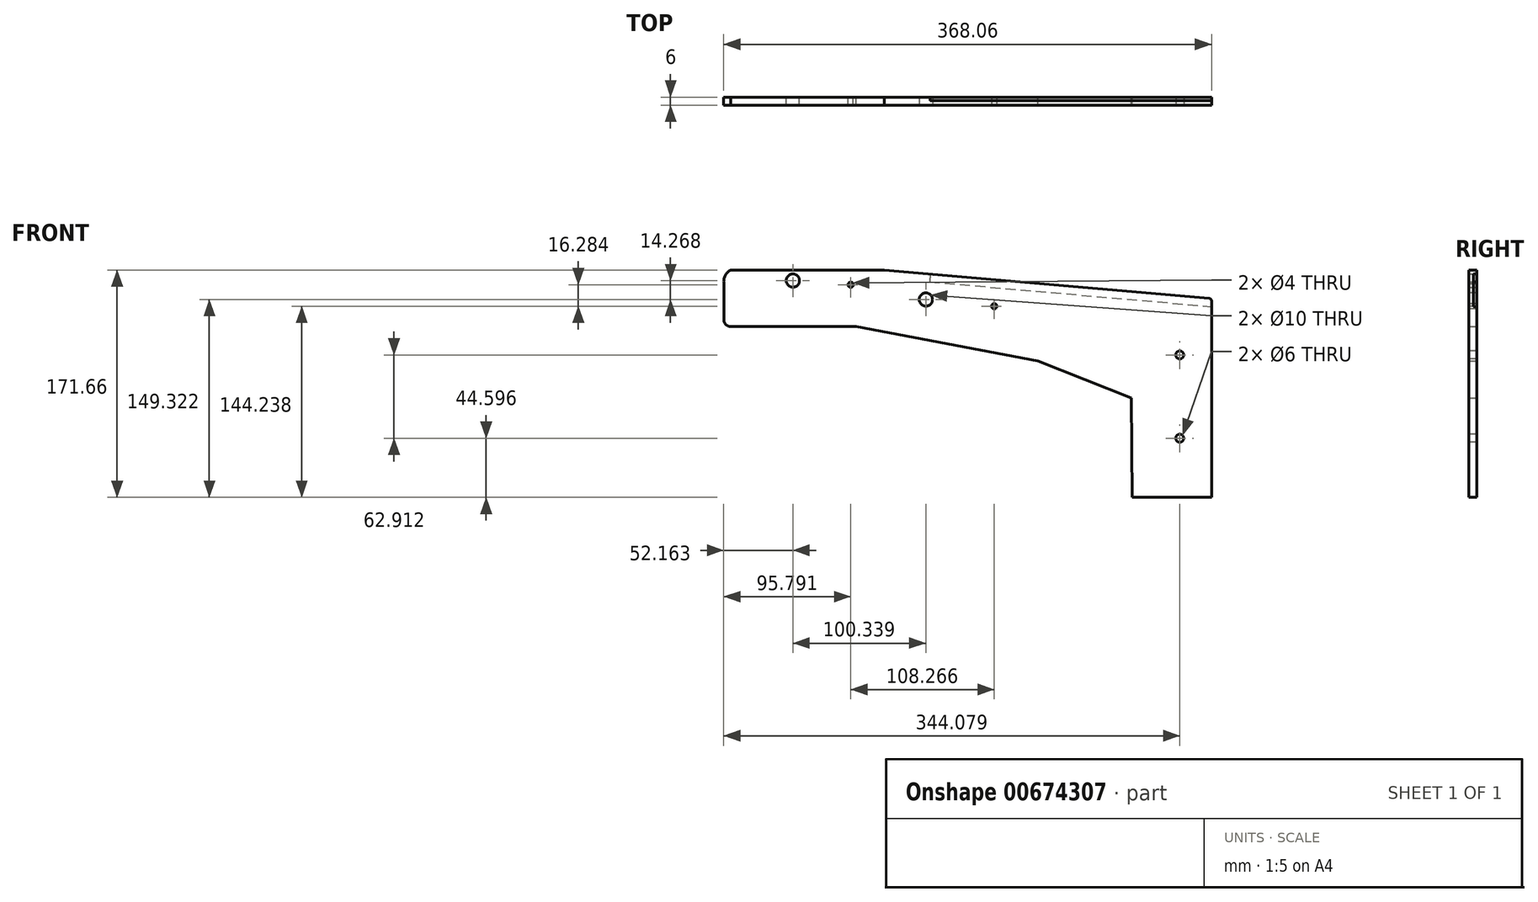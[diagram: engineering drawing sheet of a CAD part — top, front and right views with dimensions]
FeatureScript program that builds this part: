
annotation { "Feature Type Name" : "Feature", "Feature Type Description" : "" }
export const myFeature = defineFeature(function(context is Context, id is Id, definition is map)
    precondition{}
    {
        {
            var Q0;
            Q0=qCreatedBy(makeId("Front.planeOp"),FACE);
            var sketch = newSketch(context, id + "F0", { "sketchPlane" : qUnion([Q0])});
            skArc(sketch, "E0", {"start": v(-54.77, 8.07) * mm, "mid": v(-58.95, 3.73) * mm, "end": v(-59.88, -2.22) * mm});
            skLineSegment(sketch, "E1", {"start": v(-38.64, -34.67) * mm, "end": v(39.88, -34.67) * mm});
            skLineSegment(sketch, "E2", {"start": v(308.06, -13.59) * mm, "end": v(308.06, -163.59) * mm});
            skLineSegment(sketch, "E3", {"start": v(308.06, -163.59) * mm, "end": v(248.06, -163.59) * mm});
            skLineSegment(sketch, "E4", {"start": v(-59.88, -2.22) * mm, "end": v(-59.88, -29.67) * mm});
            skLineSegment(sketch, "E5", {"start": v(-54.88, -34.67) * mm, "end": v(-38.64, -34.67) * mm});
            skPoint(sketch, "E6.visualSharp", {"position": v(-59.88, -34.67) * mm});
            skArc(sketch, "E6.filletArc", {"start": v(-59.88, -29.67) * mm, "mid": v(-58.42, -33.2) * mm, "end": v(-54.88, -34.67) * mm});
            skPoint(sketch, "E7", {"position": v(35.8, -3.07) * mm});
            skCircle(sketch, "E8", {"center": v(35.8, -3.07) * mm, "radius": 2 * mm});
            skLineSegment(sketch, "E9", {"start": v(248.06, -163.59) * mm, "end": v(247.38, -88.6) * mm});
            skLineSegment(sketch, "E10", {"start": v(177.12, -60.52) * mm, "end": v(247.38, -88.6) * mm});
            skLineSegment(sketch, "E11", {"start": v(39.88, -34.67) * mm, "end": v(177.12, -60.52) * mm});
            skLineSegment(sketch, "E12", {"start": v(308.06, -13.59) * mm, "end": v(61.1, 8.07) * mm});
            skLineSegment(sketch, "E13", {"start": v(61.1, 8.07) * mm, "end": v(-54.77, 8.07) * mm});
            skSolve(sketch);
        }
        {
            var Q0;
            Q0=qSketchRegion(id+"F0",true);
            extrude(context, id + "F1", {"entities" : qUnion([Q0]), "depth" : 6 * mm, "offsetDistance" : 25 * mm});
        }
        {
            var Q0;
            Q0=makeQuery(id+"F1.opExtrude","CAP_FACE",FACE,{"disambiguationData":[OSD([sQuery(id+"F0.wireOp",EDGE,"69VMhtjD-FHem-1Nzl-ZIln-yZqZocFnkeLI"),sQuery(id+"F0.wireOp",EDGE,"E0"),sQuery(id+"F0.wireOp",EDGE,"E1"),sQuery(id+"F0.wireOp",EDGE,"E2"),sQuery(id+"F0.wireOp",EDGE,"E3"),sQuery(id+"F0.wireOp",EDGE,"zyuM4KxI-rK7D-eBj5-RQWG-Z7kNhVQKbpSr"),sQuery(id+"F0.wireOp",EDGE,"E4"),sQuery(id+"F0.wireOp",EDGE,"E5"),sQuery(id+"F0.wireOp",EDGE,"E6.filletArc"),sQuery(id+"F0.wireOp",EDGE,"Sq1smuhl-J9rg-3BfP-JIUe-rn6nJ9PzM2vD"),sQuery(id+"F0.wireOp",EDGE,"PUNmVgVp-qFH2-CwZl-KZ4H-ZFihZqVa5LSU"),sQuery(id+"F0.wireOp",EDGE,"RsVNkQyW-0Ggk-FljP-8XP7-kQ1KxApps7TM")])],"isStart":false});
            var sketch = newSketch(context, id + "F2", { "sketchPlane" : qUnion([Q0])});
            skLineSegment(sketch, "E14", {"start": v(-49.88, 0) * mm, "end": v(-59.97, 0) * mm});
            skLineSegment(sketch, "E15", {"start": v(-49.88, 0) * mm, "end": v(30.12, 0) * mm});
            skLineSegment(sketch, "E16", {"start": v(30.12, 0) * mm, "end": v(92.5, -8.77) * mm});
            skLineSegment(sketch, "E17", {"start": v(92.5, -8.77) * mm, "end": v(92.5, -14.27) * mm});
            skCircle(sketch, "E18", {"center": v(92.5, -14.27) * mm, "radius": 5 * mm});
            skSolve(sketch);
        }
        {
            var Q0;
            Q0=qSketchRegion(id+"F2",true);
            extrude(context, id + "F3", {"entities" : qUnion([Q0]), "operationType" : NewBodyOperationType.REMOVE, "endBound" : BoundingType.THROUGH_ALL, "oppositeDirection" : true, "depth" : 25 * mm, "offsetDistance" : 25 * mm});
        }
        {
            var Q0;
            Q0=makeQuery(id+"F1.opExtrude","CAP_FACE",FACE,{"disambiguationData":[OSD([sQuery(id+"F0.wireOp",EDGE,"69VMhtjD-FHem-1Nzl-ZIln-yZqZocFnkeLI"),sQuery(id+"F0.wireOp",EDGE,"E0"),sQuery(id+"F0.wireOp",EDGE,"E1"),sQuery(id+"F0.wireOp",EDGE,"E2"),sQuery(id+"F0.wireOp",EDGE,"E3"),sQuery(id+"F0.wireOp",EDGE,"zyuM4KxI-rK7D-eBj5-RQWG-Z7kNhVQKbpSr"),sQuery(id+"F0.wireOp",EDGE,"E4"),sQuery(id+"F0.wireOp",EDGE,"E5"),sQuery(id+"F0.wireOp",EDGE,"E6.filletArc"),sQuery(id+"F0.wireOp",EDGE,"Sq1smuhl-J9rg-3BfP-JIUe-rn6nJ9PzM2vD"),sQuery(id+"F0.wireOp",EDGE,"PUNmVgVp-qFH2-CwZl-KZ4H-ZFihZqVa5LSU"),sQuery(id+"F0.wireOp",EDGE,"RsVNkQyW-0Ggk-FljP-8XP7-kQ1KxApps7TM")])],"isStart":false});
            var sketch = newSketch(context, id + "F4", { "sketchPlane" : qUnion([Q0])});
            skLineSegment(sketch, "E19", {"start": v(111.32, -0.3) * mm, "end": v(111.32, -12.3) * mm});
            skCircle(sketch, "E20", {"center": v(284.08, -119) * mm, "radius": 3 * mm});
            skCircle(sketch, "E21", {"center": v(284.08, -56.08) * mm, "radius": 3 * mm});
            skLineSegment(sketch, "E22", {"start": v(284.08, -56.08) * mm, "end": v(284.08, -119) * mm});
            skSolve(sketch);
        }
        {
            var Q0;
            Q0=qSketchRegion(id+"F4",true);
            extrude(context, id + "F5", {"entities" : qUnion([Q0]), "operationType" : NewBodyOperationType.REMOVE, "endBound" : BoundingType.THROUGH_ALL, "oppositeDirection" : true, "depth" : 25 * mm, "offsetDistance" : 25 * mm});
        }
        {
            var Q0;
            Q0=makeQuery(id+"F1.opExtrude","CAP_FACE",FACE,{"disambiguationData":[OSD([sQuery(id+"F0.wireOp",EDGE,"69VMhtjD-FHem-1Nzl-ZIln-yZqZocFnkeLI"),sQuery(id+"F0.wireOp",EDGE,"E0"),sQuery(id+"F0.wireOp",EDGE,"E1"),sQuery(id+"F0.wireOp",EDGE,"E2"),sQuery(id+"F0.wireOp",EDGE,"E3"),sQuery(id+"F0.wireOp",EDGE,"zyuM4KxI-rK7D-eBj5-RQWG-Z7kNhVQKbpSr"),sQuery(id+"F0.wireOp",EDGE,"E4"),sQuery(id+"F0.wireOp",EDGE,"E5"),sQuery(id+"F0.wireOp",EDGE,"E6.filletArc"),sQuery(id+"F0.wireOp",EDGE,"Sq1smuhl-J9rg-3BfP-JIUe-rn6nJ9PzM2vD"),sQuery(id+"F0.wireOp",EDGE,"PUNmVgVp-qFH2-CwZl-KZ4H-ZFihZqVa5LSU"),sQuery(id+"F0.wireOp",EDGE,"RsVNkQyW-0Ggk-FljP-8XP7-kQ1KxApps7TM")])],"isStart":true});
            var sketch = newSketch(context, id + "F6", { "sketchPlane" : qUnion([Q0])});
            skCircle(sketch, "E23", {"center": v(7.84, 0) * mm, "radius": 5 * mm});
            skSolve(sketch);
        }
        {
            var Q0;
            Q0=qSketchRegion(id+"F6",true);
            extrude(context, id + "F7", {"entities" : qUnion([Q0]), "operationType" : NewBodyOperationType.REMOVE, "endBound" : BoundingType.THROUGH_ALL, "oppositeDirection" : true, "depth" : 25 * mm, "offsetDistance" : 25 * mm});
        }
        {
            var Q0;
            Q0 = qSketchRegion(id + "F0", true);
            extrude(context, id + "F8", {"entities" : qUnion([Q0]), "operationType" : NewBodyOperationType.REMOVE, "endBound" : BoundingType.THROUGH_ALL, "oppositeDirection" : true, "depth" : 25 * mm, "offsetDistance" : 25 * mm});
        }
        {
            var Q0;
            Q0=makeQuery(id+"F1.opExtrude","CAP_FACE",FACE,{"disambiguationData":[OSD([sQuery(id+"F0.wireOp",EDGE,"69VMhtjD-FHem-1Nzl-ZIln-yZqZocFnkeLI"),sQuery(id+"F0.wireOp",EDGE,"E0"),sQuery(id+"F0.wireOp",EDGE,"E1"),sQuery(id+"F0.wireOp",EDGE,"E2"),sQuery(id+"F0.wireOp",EDGE,"E3"),sQuery(id+"F0.wireOp",EDGE,"zyuM4KxI-rK7D-eBj5-RQWG-Z7kNhVQKbpSr"),sQuery(id+"F0.wireOp",EDGE,"E4"),sQuery(id+"F0.wireOp",EDGE,"E5"),sQuery(id+"F0.wireOp",EDGE,"E6.filletArc"),sQuery(id+"F0.wireOp",EDGE,"Sq1smuhl-J9rg-3BfP-JIUe-rn6nJ9PzM2vD"),sQuery(id+"F0.wireOp",EDGE,"PUNmVgVp-qFH2-CwZl-KZ4H-ZFihZqVa5LSU"),sQuery(id+"F0.wireOp",EDGE,"RsVNkQyW-0Ggk-FljP-8XP7-kQ1KxApps7TM"),sQuery(id+"F0.wireOp",EDGE,"E8")])],"isStart":false});
            var sketch = newSketch(context, id + "F9", { "sketchPlane" : qUnion([Q0])});
            skPoint(sketch, "E24", {"position": v(144.06, -19.35) * mm});
            skCircle(sketch, "E25", {"center": v(144.06, -19.35) * mm, "radius": 2 * mm});
            skSolve(sketch);
        }
        {
            var Q0;
            Q0 = qSketchRegion(id + "F9", true);
            extrude(context, id + "F10", {"entities" : qUnion([Q0]), "operationType" : NewBodyOperationType.REMOVE, "endBound" : BoundingType.THROUGH_ALL, "oppositeDirection" : true, "depth" : 25 * mm, "offsetDistance" : 25 * mm});
        }
        {
            var Q0;
            Q0=makeQuery(id+"F1.opExtrude","CAP_FACE",FACE,{"disambiguationData":[OSD([sQuery(id+"F0.wireOp",EDGE,"E0"),sQuery(id+"F0.wireOp",EDGE,"E1"),sQuery(id+"F0.wireOp",EDGE,"E2"),sQuery(id+"F0.wireOp",EDGE,"E3"),sQuery(id+"F0.wireOp",EDGE,"E4"),sQuery(id+"F0.wireOp",EDGE,"E5"),sQuery(id+"F0.wireOp",EDGE,"E6.filletArc"),sQuery(id+"F0.wireOp",EDGE,"E8"),sQuery(id+"F0.wireOp",EDGE,"E9"),sQuery(id+"F0.wireOp",EDGE,"E10"),sQuery(id+"F0.wireOp",EDGE,"E11"),sQuery(id+"F0.wireOp",EDGE,"E12"),sQuery(id+"F0.wireOp",EDGE,"E13")])],"isStart":true});
            var sketch = newSketch(context, id + "F11", { "sketchPlane" : qUnion([Q0])});
            skPoint(sketch, "E26.start.orphan", {"position": v(-95.9, 5.01) * mm});
            skLineSegment(sketch, "E27", {"start": v(-95.9, 5.01) * mm, "end": v(-298.13, -12.71) * mm});
            skLineSegment(sketch, "E28", {"start": v(-95.38, -0.96) * mm, "end": v(-297.6, -18.7) * mm});
            skLineSegment(sketch, "E29", {"start": v(-95.9, 5.01) * mm, "end": v(-95.38, -0.96) * mm});
            skLineSegment(sketch, "E30", {"start": v(-298.13, -12.71) * mm, "end": v(-308.06, -13.59) * mm});
            skLineSegment(sketch, "E31", {"start": v(-297.6, -18.7) * mm, "end": v(-308.06, -19.6) * mm});
            skLineSegment(sketch, "E32", {"start": v(-308.06, -19.6) * mm, "end": v(-308.06, -13.59) * mm});
            skSolve(sketch);
        }
        {
            var Q0;
            Q0 = qSketchRegion(id + "F11", true);
            extrude(context, id + "F12", {"entities" : qUnion([Q0]), "operationType" : NewBodyOperationType.REMOVE, "oppositeDirection" : true, "depth" : 2.5 * mm, "offsetDistance" : 25 * mm});
        }
        {
            var Q0;
            Q0=makeQuery(id+"F1.opExtrude","SWEPT_EDGE",EDGE,{"disambiguationData":[OSD([sQuery(id+"F0.wireOp",EDGE,"E2"),sQuery(id+"F0.wireOp",EDGE,"E12")])]});
            fillet(context, id + "F13", {"entities" : qUnion([Q0]), "radius" : 2 * mm, "tangentPropagation" : true, "allowEdgeOverflow" : false});
        }
    });
